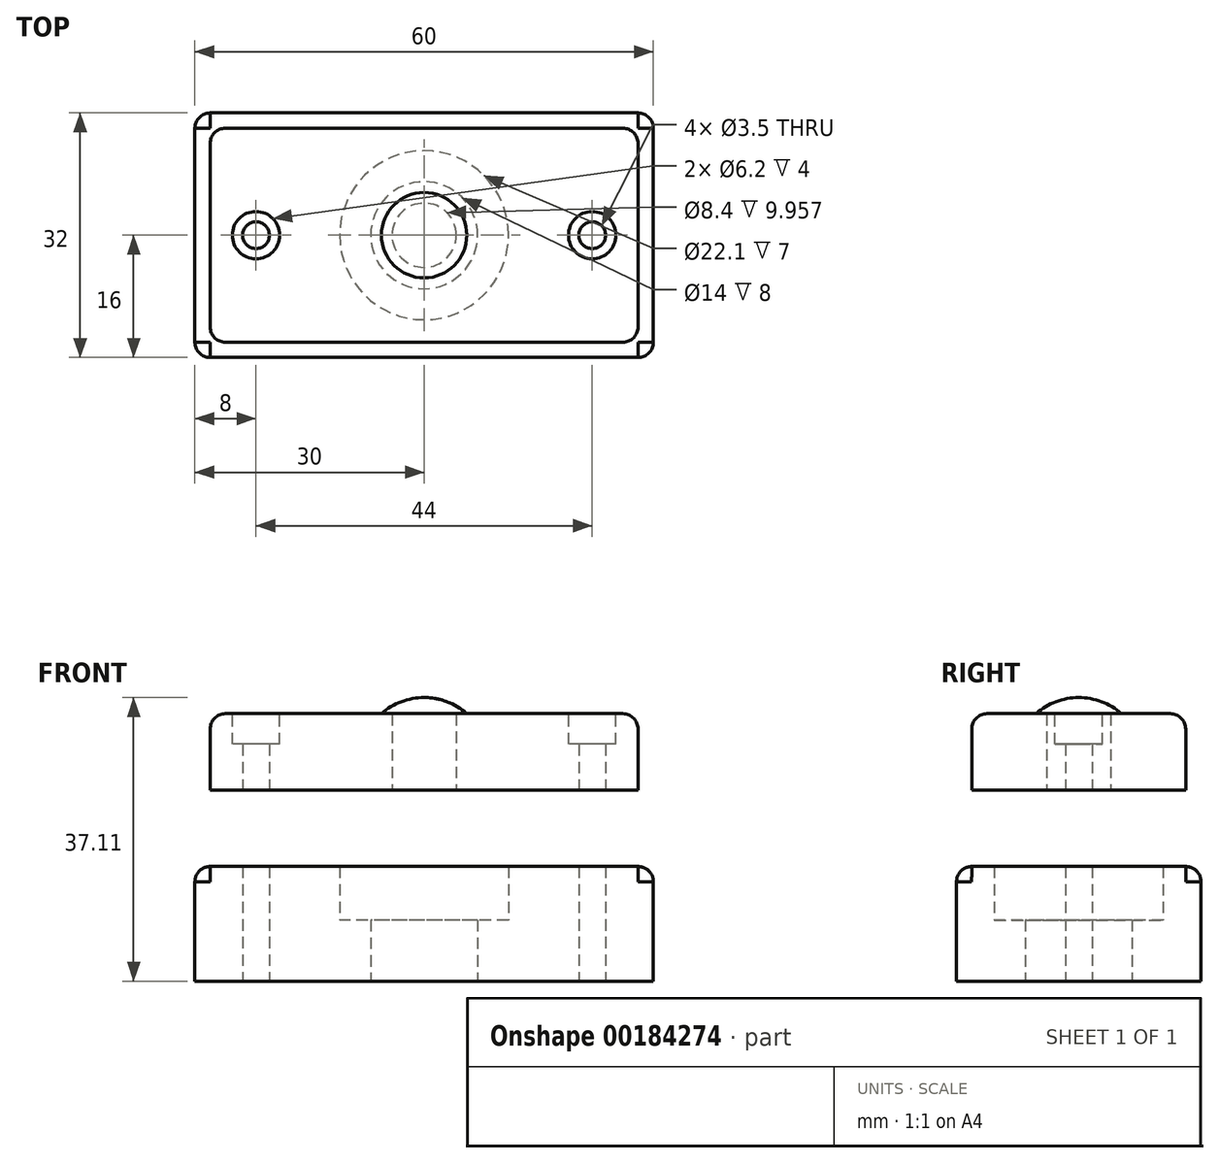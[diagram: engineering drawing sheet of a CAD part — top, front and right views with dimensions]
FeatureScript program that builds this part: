
annotation { "Feature Type Name" : "Feature", "Feature Type Description" : "" }
export const myFeature = defineFeature(function(context is Context, id is Id, definition is map)
    precondition{}
    {
        {
            var Q0;
            Q0=qCreatedBy(makeId("Top.planeOp"),FACE);
            var sketch = newSketch(context, id + "F0", { "sketchPlane" : qUnion([Q0])});
            skLineSegment(sketch, "E0.bottom", {"start": v(-28.01, 16) * mm, "end": v(28.01, 16) * mm});
            skLineSegment(sketch, "E0.top", {"start": v(-28.01, -16) * mm, "end": v(28.01, -16) * mm});
            skLineSegment(sketch, "E0.left", {"start": v(-30, 14.01) * mm, "end": v(-30, -14.01) * mm});
            skLineSegment(sketch, "E0.right", {"start": v(30, 14.01) * mm, "end": v(30, -14.01) * mm});
            skCircle(sketch, "E1", {"center": v(0, 0) * mm, "radius": 11.05 * mm});
            skCircle(sketch, "E2", {"center": v(-22, 0) * mm, "radius": 1.75 * mm});
            skCircle(sketch, "E3.MirrorC", {"center": v(22, 0) * mm, "radius": 1.75 * mm});
            skArc(sketch, "E4", {"start": v(-28.01, 16) * mm, "mid": v(-29.42, 15.42) * mm, "end": v(-30, 14.01) * mm});
            skArc(sketch, "E5", {"start": v(-30, -14.01) * mm, "mid": v(-29.42, -15.42) * mm, "end": v(-28.01, -16) * mm});
            skArc(sketch, "E6", {"start": v(28.01, -16) * mm, "mid": v(29.42, -15.42) * mm, "end": v(30, -14.01) * mm});
            skArc(sketch, "E7", {"start": v(30, 14.01) * mm, "mid": v(29.42, 15.42) * mm, "end": v(28.01, 16) * mm});
            skCircle(sketch, "E8", {"center": v(0, 0) * mm, "radius": 7 * mm});
            skSolve(sketch);
        }
        {
            var Q0;
            Q0=makeQuery(id+"F0.imprint","IMPRINT",FACE,{"disambiguationData":[TD([[makeQuery(id+"F0.imprint","IMPRINT",EDGE,{"derivedFrom":sQuery(id+"F0.wireOp",EDGE,"E0.bottom")}),-1.0]])]});
            extrude(context, id + "F1", {"entities" : qUnion([Q0]), "depth" : 15 * mm});
        }
        {
            var Q0;
            Q0=makeQuery(id+"F0.imprint","IMPRINT",FACE,{"disambiguationData":[TD([[makeQuery(id+"F0.imprint","IMPRINT",EDGE,{"derivedFrom":sQuery(id+"F0.wireOp",EDGE,"E1")}),1.0]])]});
            extrude(context, id + "F2", {"entities" : qUnion([Q0]), "operationType" : NewBodyOperationType.ADD, "depth" : 8 * mm});
        }
        {
            var Q0;
            Q0=qCreatedBy(makeId("Top.planeOp"),FACE);
            cPlane(context, id + "F3", {"entities" : qUnion([Q0]), "cplaneType" : CPlaneType.OFFSET, "offset" : 25 * mm, "width" : 150 * mm, "height" : 150 * mm});
        }
        {
            var Q0;
            Q0=qCreatedBy(id+"F3.planeOp",FACE);
            var sketch = newSketch(context, id + "F4", { "sketchPlane" : qUnion([Q0])});
            skLineSegment(sketch, "E9.bottom", {"start": v(-28, 14) * mm, "end": v(28, 14) * mm});
            skLineSegment(sketch, "E9.top", {"start": v(-28, -14) * mm, "end": v(28, -14) * mm});
            skLineSegment(sketch, "E9.left", {"start": v(-28, 14) * mm, "end": v(-28, -14) * mm});
            skLineSegment(sketch, "E9.right", {"start": v(28, 14) * mm, "end": v(28, -14) * mm});
            skCircle(sketch, "E10", {"center": v(-22, 0) * mm, "radius": 1.75 * mm});
            skCircle(sketch, "E11", {"center": v(22, 0) * mm, "radius": 1.75 * mm});
            skCircle(sketch, "E12", {"center": v(0, 0) * mm, "radius": 4.2 * mm});
            skSolve(sketch);
        }
        {
            var Q0;
            Q0=makeQuery(id+"F4.imprint","IMPRINT",FACE,{"disambiguationData":[TD([[makeQuery(id+"F4.imprint","IMPRINT",EDGE,{"derivedFrom":sQuery(id+"F4.wireOp",EDGE,"E9.bottom")}),-1.0]])]});
            var Q1;
            Q1=makeQuery(id+"F4.imprint","IMPRINT",FACE,{"disambiguationData":[TD([[makeQuery(id+"F4.imprint","IMPRINT",EDGE,{"derivedFrom":makeQuery(id+"F1.opExtrude","CAP_EDGE",EDGE,{"disambiguationData":[OSD([sQuery(id+"F0.wireOp",EDGE,"E1")])],"isStart":false})}),1.0]])]});
            var Q2;
            Q2=makeQuery(id+"F4.imprint","IMPRINT",FACE,{"disambiguationData":[TD([[makeQuery(id+"F4.imprint","IMPRINT",EDGE,{"derivedFrom":sQuery(id+"F4.wireOp",EDGE,"7qTocK3T-U29J-NfhJ-00Gf-MRpjMCliMGuo")}),1.0]])]});
            var Q3;
            Q3=makeQuery(id+"F4.imprint","IMPRINT",FACE,{"disambiguationData":[TD([[makeQuery(id+"F4.imprint","IMPRINT",EDGE,{"derivedFrom":sQuery(id+"F4.wireOp",EDGE,"K9t4jXKc-Vu1R-MHHc-YyF5-x4wLlgkyiMZH")}),1.0]])]});
            var Q4;
            Q4=makeQuery(id+"F4.imprint","IMPRINT",FACE,{"disambiguationData":[TD([[makeQuery(id+"F4.imprint","IMPRINT",EDGE,{"derivedFrom":sQuery(id+"F4.wireOp",EDGE,"E12")}),1.0]])]});
            extrude(context, id + "F5", {"entities" : qUnion([Q0, Q1, Q2, Q3, Q4]), "operationType" : NewBodyOperationType.ADD, "depth" : 10 * mm});
        }
        {
            var Q0;
            Q0=makeQuery(id+"F5.opExtrude","CAP_EDGE",EDGE,{"disambiguationData":[OSD([sQuery(id+"F4.wireOp",EDGE,"E9.top")])],"isStart":false});
            var Q1;
            Q1=makeQuery(id+"F5.opExtrude","CAP_EDGE",EDGE,{"disambiguationData":[OSD([sQuery(id+"F4.wireOp",EDGE,"E9.right")])],"isStart":false});
            var Q2;
            Q2=makeQuery(id+"F5.opExtrude","CAP_EDGE",EDGE,{"disambiguationData":[OSD([sQuery(id+"F4.wireOp",EDGE,"E9.bottom")])],"isStart":false});
            var Q3;
            Q3=makeQuery(id+"F5.opExtrude","CAP_EDGE",EDGE,{"disambiguationData":[OSD([sQuery(id+"F4.wireOp",EDGE,"E9.left")])],"isStart":false});
            var Q4;
            Q4=makeQuery(id+"F5.opExtrude","SWEPT_EDGE",EDGE,{"disambiguationData":[OSD([sQuery(id+"F4.wireOp",EDGE,"E9.top"),sQuery(id+"F4.wireOp",EDGE,"E9.left")])]});
            var Q5;
            Q5=makeQuery(id+"F5.opExtrude","SWEPT_EDGE",EDGE,{"disambiguationData":[OSD([sQuery(id+"F4.wireOp",EDGE,"E9.bottom"),sQuery(id+"F4.wireOp",EDGE,"E9.left")])]});
            var Q6;
            Q6=makeQuery(id+"F5.opExtrude","SWEPT_EDGE",EDGE,{"disambiguationData":[OSD([sQuery(id+"F4.wireOp",EDGE,"E9.top"),sQuery(id+"F4.wireOp",EDGE,"E9.right")])]});
            var Q7;
            Q7=makeQuery(id+"F5.opExtrude","SWEPT_EDGE",EDGE,{"disambiguationData":[OSD([sQuery(id+"F4.wireOp",EDGE,"E9.bottom"),sQuery(id+"F4.wireOp",EDGE,"E9.right")])]});
            fillet(context, id + "F6", {"entities" : qUnion([Q0, Q1, Q2, Q3, Q4, Q5, Q6, Q7]), "radius" : 2 * mm, "tangentPropagation" : true, "allowEdgeOverflow" : false});
        }
        {
            var Q0;
            Q0=makeQuery(id+"F4.imprint","IMPRINT",FACE,{"disambiguationData":[TD([[makeQuery(id+"F4.imprint","IMPRINT",EDGE,{"derivedFrom":sQuery(id+"F4.wireOp",EDGE,"E12")}),1.0]])]});
            extrude(context, id + "F7", {"entities" : qUnion([Q0]), "operationType" : NewBodyOperationType.REMOVE, "depth" : 10 * mm});
        }
        {
            var Q0;
            Q0=makeQuery(id+"F1.opExtrude","CAP_EDGE",EDGE,{"disambiguationData":[OSD([sQuery(id+"F0.wireOp",EDGE,"E0.top")])],"isStart":false});
            fillet(context, id + "F8", {"entities" : qUnion([Q0]), "radius" : 2 * mm, "tangentPropagation" : true, "allowEdgeOverflow" : false});
        }
        {
            var Q0;
            Q0=makeQuery(id+"F5.opExtrude","CAP_FACE",FACE,{"disambiguationData":[OSD([sQuery(id+"F4.wireOp",EDGE,"E9.bottom"),sQuery(id+"F4.wireOp",EDGE,"E9.top"),sQuery(id+"F4.wireOp",EDGE,"E9.left"),sQuery(id+"F4.wireOp",EDGE,"E9.right"),sQuery(id+"F4.wireOp",EDGE,"E10"),sQuery(id+"F4.wireOp",EDGE,"E11")])],"isStart":false});
            var sketch = newSketch(context, id + "F9", { "sketchPlane" : qUnion([Q0])});
            skCircle(sketch, "E13", {"center": v(-22, 0) * mm, "radius": 3.1 * mm});
            skCircle(sketch, "E14", {"center": v(22, 0) * mm, "radius": 3.1 * mm});
            skSolve(sketch);
        }
        {
            var Q0;
            Q0=makeQuery(id+"F9.imprint","IMPRINT",FACE,{"disambiguationData":[TD([[makeQuery(id+"F9.imprint","IMPRINT",EDGE,{"derivedFrom":sQuery(id+"F9.wireOp",EDGE,"E13")}),1.0]])]});
            var Q1;
            Q1=makeQuery(id+"F9.imprint","IMPRINT",FACE,{"disambiguationData":[TD([[makeQuery(id+"F9.imprint","IMPRINT",EDGE,{"derivedFrom":sQuery(id+"F9.wireOp",EDGE,"E14")}),1.0]])]});
            extrude(context, id + "F10", {"entities" : qUnion([Q0, Q1]), "operationType" : NewBodyOperationType.REMOVE, "oppositeDirection" : true, "depth" : 4 * mm});
        }
        {
            var Q0;
            Q0=qCreatedBy(makeId("Front.planeOp"),FACE);
            var sketch = newSketch(context, id + "F11", { "sketchPlane" : qUnion([Q0])});
            skArc(sketch, "E15", {"start": v(5.63, 34.96) * mm, "mid": v(3.02, 36.55) * mm, "end": v(0, 37.1) * mm});
            skLineSegment(sketch, "E16", {"start": v(0, 34.96) * mm, "end": v(5.63, 34.96) * mm});
            skLineSegment(sketch, "E17", {"start": v(0, 37.1) * mm, "end": v(0, 34.96) * mm});
            skPoint(sketch, "E18.orphan", {"position": v(-5.63, 34.96) * mm});
            skSolve(sketch);
        }
        {
            var Q0;
            Q0=makeQuery(id+"F11.imprint","IMPRINT",FACE,{"disambiguationData":[TD([[makeQuery(id+"F11.imprint","IMPRINT",EDGE,{"derivedFrom":sQuery(id+"F11.wireOp",EDGE,"E15")}),1.0]])]});
            var Q1;
            Q1=sQuery(id+"F11.wireOp",EDGE,"E17");
            revolve(context, id + "F12", {"operationType" : NewBodyOperationType.ADD, "entities" : qUnion([Q0]), "axis" : qUnion([Q1]), "revolveType" : RevolveType.FULL});
        }
    });
